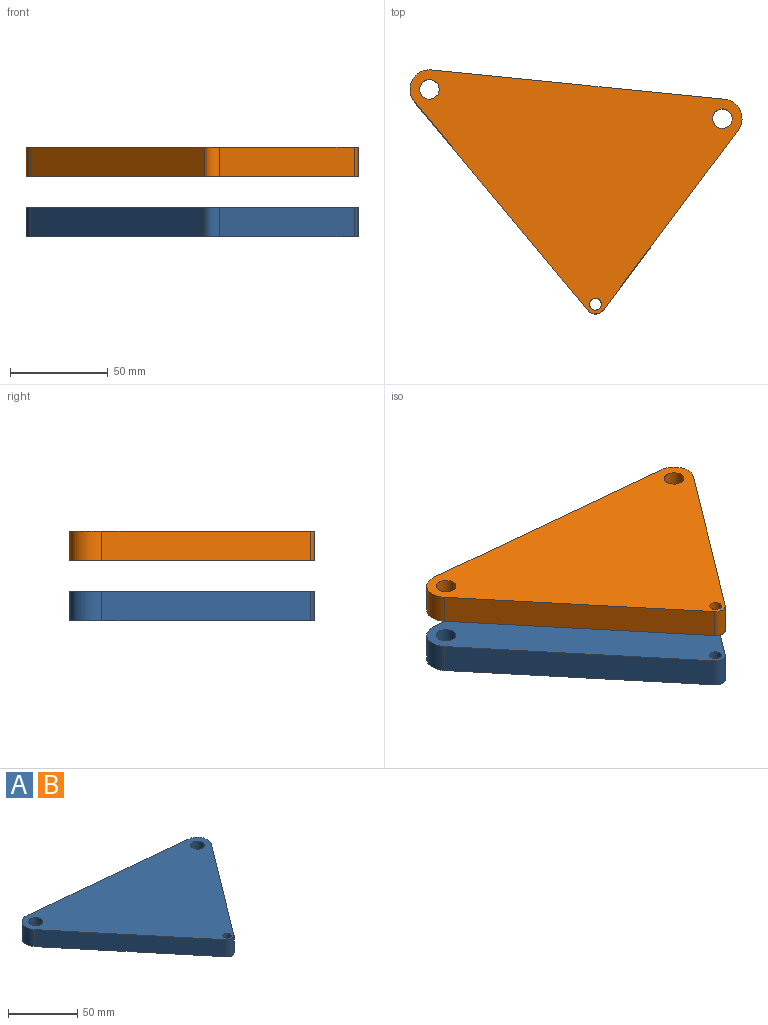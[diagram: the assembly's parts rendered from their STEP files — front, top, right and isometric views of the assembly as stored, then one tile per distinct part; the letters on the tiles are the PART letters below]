
ASSEMBLY  parts=2 mates=2
PART A: 11 faces, bbox 170x125x15 mm
  f0: plane 92x69mm, normal (0.8,-0.6,0), area 1725mm2, adj f1,f8,f9,f10
  f1: cylinder r=10mm len=15.95mm, axis (0,0,-1), area 317.2mm2, adj f0,f2,f9,f10
  f2: plane 150x15mm, normal (0.1,1,0), area 2261.2mm2, adj f1,f3,f9,f10
  f3: cylinder r=10mm len=16.4mm, axis (0,0,-1), area 354.6mm2, adj f2,f4,f9,f10
  f4: plane 106.8x88.84mm, normal (-0.77,-0.64,0), area 2083.9mm2, adj f3,f8,f9,f10
  f5: cylinder r=5mm len=15mm, axis (0,0,-1), area 471.2mm2, adj f9,f10
  f6: cylinder r=5mm len=15mm, axis (0,0,-1), area 471.2mm2, adj f9,f10
  f7: cylinder r=3mm len=15mm, axis (0,0,-1), area 282.7mm2, adj f9,f10
  f8: cylinder r=5mm len=15mm, axis (0,0,-1), area 135.3mm2, adj f0,f4,f9,f10
  f9: plane 170x125mm, normal (0,0,1), area 11085.6mm2, adj f0,f1,f2,f3,f4,f5,f6,f7
  f10: plane 170x125mm, normal (0,0,-1), area 11085.6mm2, adj f0,f1,f2,f3,f4,f5,f6,f7
PART B: same geometry as A
PLACE A t=(195.96,414.29,-671.85)mm
PLACE B t=(195.96,414.29,-640.97)mm
MATE planar A.f2 <-> B.f2  axis (0.1,1,0) through (271.96,416.74,-664.35)mm
MATE cylindrical B.f1 <-> A.f1  axis (0,0,-1) through (345.96,399.29,-625.97)mm
